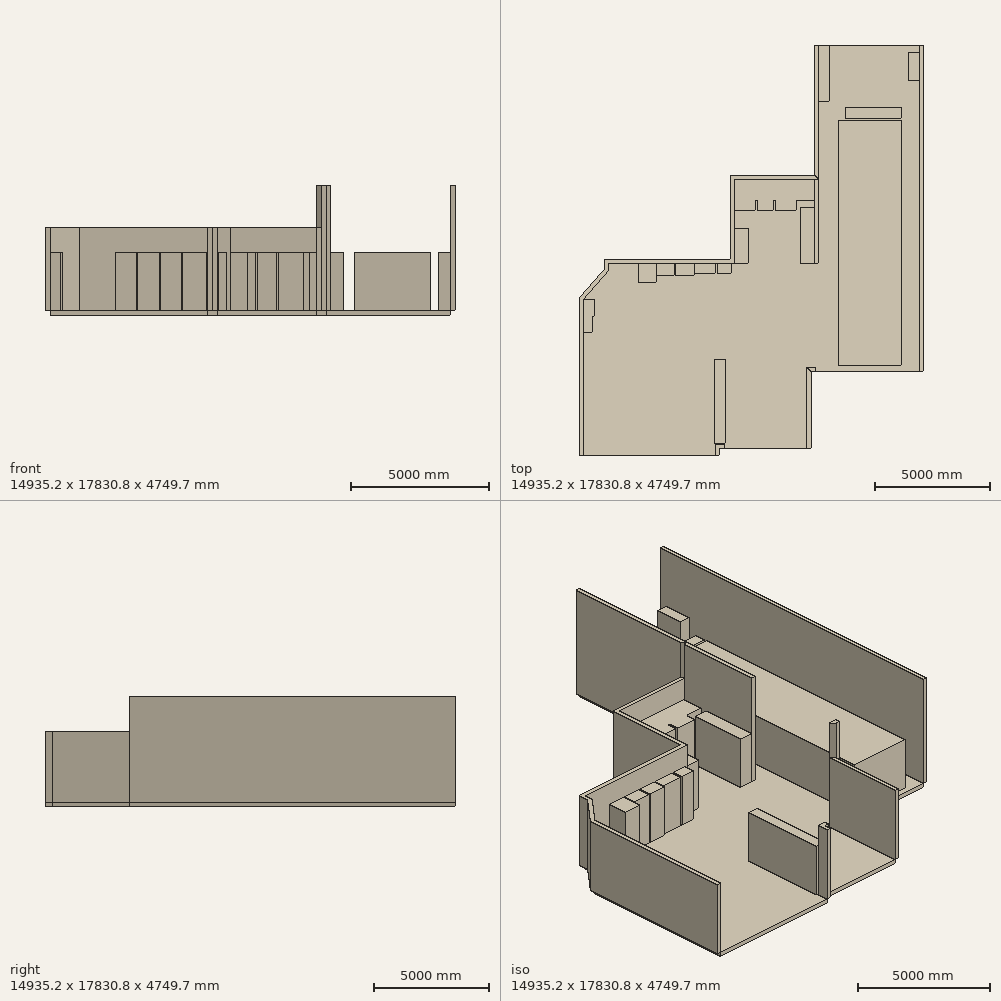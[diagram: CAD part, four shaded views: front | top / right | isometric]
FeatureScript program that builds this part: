
annotation { "Feature Type Name" : "Feature", "Feature Type Description" : "" }
export const myFeature = defineFeature(function(context is Context, id is Id, definition is map)
    precondition{}
    {
        {
            var Q0;
            Q0=qCreatedBy(makeId("Top.planeOp"),FACE);
            var sketch = newSketch(context, id + "F0", { "sketchPlane" : qUnion([Q0])});
            skLineSegment(sketch, "E0", {"start": v(0, 0) * mm, "end": v(6096, 0) * mm});
            skLineSegment(sketch, "E1", {"start": v(6096, 0) * mm, "end": v(6096, 304.8) * mm});
            skLineSegment(sketch, "E2", {"start": v(6096, 304.8) * mm, "end": v(10058.4, 304.8) * mm});
            skLineSegment(sketch, "E3", {"start": v(10058.4, 304.8) * mm, "end": v(10058.4, 3657.6) * mm});
            skLineSegment(sketch, "E4", {"start": v(10058.4, 3657.6) * mm, "end": v(14935.2, 3657.6) * mm});
            skLineSegment(sketch, "E5", {"start": v(14935.2, 3657.6) * mm, "end": v(14935.2, 17830.8) * mm});
            skLineSegment(sketch, "E6", {"start": v(14935.2, 17830.8) * mm, "end": v(10210.8, 17830.8) * mm});
            skLineSegment(sketch, "E7", {"start": v(10210.8, 17830.8) * mm, "end": v(10210.8, 12192) * mm});
            skLineSegment(sketch, "E8", {"start": v(10210.8, 12192) * mm, "end": v(6553.2, 12192) * mm});
            skLineSegment(sketch, "E9", {"start": v(6553.2, 12192) * mm, "end": v(6553.2, 8534.4) * mm});
            skLineSegment(sketch, "E10", {"start": v(0, 6858) * mm, "end": v(0, 0) * mm});
            skLineSegment(sketch, "E11", {"start": v(0, 6858) * mm, "end": v(1066.8, 8077.2) * mm});
            skLineSegment(sketch, "E12", {"start": v(1066.8, 8077.2) * mm, "end": v(1066.8, 8534.4) * mm});
            skLineSegment(sketch, "E13", {"start": v(1066.8, 8534.4) * mm, "end": v(6553.2, 8534.4) * mm});
            skLineSegment(sketch, "E14", {"start": v(177.7, 0) * mm, "end": v(177.7, 6791.23) * mm});
            skLineSegment(sketch, "E15", {"start": v(177.7, 6791.23) * mm, "end": v(1244.5, 8010.43) * mm});
            skLineSegment(sketch, "E16", {"start": v(1244.5, 8010.43) * mm, "end": v(1244.5, 8356.7) * mm});
            skLineSegment(sketch, "E17", {"start": v(1244.5, 8356.7) * mm, "end": v(6730.9, 8356.7) * mm});
            skLineSegment(sketch, "E18", {"start": v(6730.9, 8356.7) * mm, "end": v(6730.9, 12014.3) * mm});
            skLineSegment(sketch, "E19", {"start": v(6730.9, 12014.3) * mm, "end": v(10388.5, 12014.3) * mm});
            skLineSegment(sketch, "E20", {"start": v(10388.5, 12014.3) * mm, "end": v(10388.5, 17830.8) * mm});
            skLineSegment(sketch, "E21", {"start": v(10388.5, 17830.8) * mm, "end": v(14757.5, 17830.8) * mm});
            skLineSegment(sketch, "E22", {"start": v(9880.7, 3835.3) * mm, "end": v(9880.7, 304.8) * mm});
            skLineSegment(sketch, "E23", {"start": v(9880.7, 304.8) * mm, "end": v(6273.7, 304.8) * mm});
            skLineSegment(sketch, "E24", {"start": v(6273.7, 304.8) * mm, "end": v(6273.7, 482.5) * mm});
            skLineSegment(sketch, "E25", {"start": v(6273.7, 482.5) * mm, "end": v(5918.3, 482.5) * mm});
            skLineSegment(sketch, "E26", {"start": v(5918.3, 482.5) * mm, "end": v(5918.3, 0) * mm});
            skLineSegment(sketch, "E27", {"start": v(5918.3, 0) * mm, "end": v(177.7, 0) * mm});
            skLineSegment(sketch, "E28", {"start": v(14757.5, 17830.8) * mm, "end": v(14757.5, 3657.6) * mm});
            skLineSegment(sketch, "E29", {"start": v(14757.5, 3657.6) * mm, "end": v(10236.1, 3657.6) * mm});
            skLineSegment(sketch, "E30", {"start": v(10236.1, 3657.6) * mm, "end": v(10236.1, 3835.3) * mm});
            skLineSegment(sketch, "E31", {"start": v(10236.1, 3835.3) * mm, "end": v(9880.7, 3835.3) * mm});
            skLineSegment(sketch, "E32", {"start": v(10210.8, 12192) * mm, "end": v(10388.5, 12014.3) * mm});
            skLineSegment(sketch, "E33", {"start": v(10058.4, 3657.6) * mm, "end": v(9880.7, 3835.3) * mm});
            skLineSegment(sketch, "E34.bottom", {"start": v(10388.5, 12014.3) * mm, "end": v(10210.8, 12014.3) * mm});
            skLineSegment(sketch, "E34.top", {"start": v(10388.5, 8356.7) * mm, "end": v(10210.8, 8356.7) * mm});
            skLineSegment(sketch, "E34.left", {"start": v(10388.5, 12014.3) * mm, "end": v(10388.5, 8356.7) * mm});
            skLineSegment(sketch, "E34.right", {"start": v(10210.8, 12014.3) * mm, "end": v(10210.8, 8356.7) * mm});
            skSolve(sketch);
        }
        {
            var Q0;
            Q0=makeQuery(id+"F0.imprint","IMPRINT",FACE,{"disambiguationData":[TD([[makeQuery(id+"F0.imprint","IMPRINT",EDGE,{"derivedFrom":sQuery(id+"F0.wireOp",EDGE,"E8")}),1.0]])]});
            var Q1;
            {var subQ2=sQuery(id+"F0.wireOp",EDGE,"E1");Q1=makeQuery(id+"F0.imprint","IMPRINT",FACE,{"disambiguationData":[TD([[makeQuery(id+"F0.imprint","IMPRINT",EDGE,{"derivedFrom":subQ2}),1.0]])]});}
            var Q2;
            {var subQ0=sQuery(id+"F0.wireOp",EDGE,"E3");Q2=makeQuery(id+"F0.imprint","IMPRINT",FACE,{"disambiguationData":[TD([[makeQuery(id+"F0.imprint","IMPRINT",EDGE,{"derivedFrom":subQ0}),1.0]])]});}
            extrude(context, id + "F1", {"entities" : qUnion([Q0, Q1, Q2]), "depth" : 3048 * mm, "offsetDistance" : 30.48 * mm});
        }
        {
            var Q0;
            {var subQ0=sQuery(id+"F0.wireOp",EDGE,"E5");Q0=makeQuery(id+"F0.imprint","IMPRINT",FACE,{"disambiguationData":[TD([[makeQuery(id+"F0.imprint","IMPRINT",EDGE,{"derivedFrom":subQ0}),1.0]])]});}
            var Q1;
            {var subQ2=sQuery(id+"F0.wireOp",EDGE,"E30");Q1=makeQuery(id+"F0.imprint","IMPRINT",FACE,{"disambiguationData":[TD([[makeQuery(id+"F0.imprint","IMPRINT",EDGE,{"derivedFrom":subQ2}),1.0]])]});}
            var Q2;
            {var subQ0=sQuery(id+"F0.wireOp",EDGE,"E7");Q2=makeQuery(id+"F0.imprint","IMPRINT",FACE,{"disambiguationData":[TD([[makeQuery(id+"F0.imprint","IMPRINT",EDGE,{"derivedFrom":subQ0}),1.0]])]});}
            var Q3;
            Q3=makeQuery(id+"F0.imprint","IMPRINT",FACE,{"disambiguationData":[TD([[makeQuery(id+"F0.imprint","IMPRINT",EDGE,{"derivedFrom":sQuery(id+"F0.wireOp",EDGE,"E34.top")}),-1.0]])]});
            extrude(context, id + "F2", {"entities" : qUnion([Q0, Q1, Q2, Q3]), "depth" : 4572 * mm, "offsetDistance" : 30.48 * mm});
        }
        {
            var Q0;
            {var subQ6=sQuery(id+"F0.wireOp",EDGE,"E14");Q0=makeQuery(id+"F0.imprint","IMPRINT",FACE,{"disambiguationData":[TD([[makeQuery(id+"F0.imprint","IMPRINT",EDGE,{"derivedFrom":subQ6}),-1.0]])]});}
            extrude(context, id + "F3", {"entities" : qUnion([Q0]), "oppositeDirection" : true, "depth" : 177.7 * mm, "offsetDistance" : 30.48 * mm});
        }
        {
            var Q0;
            Q0=makeQuery(id+"F3.opExtrude","CAP_FACE",FACE,{"disambiguationData":[OSD([sQuery(id+"F0.wireOp",EDGE,"E0"),sQuery(id+"F0.wireOp",EDGE,"E2"),sQuery(id+"F0.wireOp",EDGE,"E4"),sQuery(id+"F0.wireOp",EDGE,"E6"),sQuery(id+"F0.wireOp",EDGE,"E14"),sQuery(id+"F0.wireOp",EDGE,"E15"),sQuery(id+"F0.wireOp",EDGE,"E16"),sQuery(id+"F0.wireOp",EDGE,"E17"),sQuery(id+"F0.wireOp",EDGE,"E18"),sQuery(id+"F0.wireOp",EDGE,"E19"),sQuery(id+"F0.wireOp",EDGE,"E20"),sQuery(id+"F0.wireOp",EDGE,"E22"),sQuery(id+"F0.wireOp",EDGE,"E24"),sQuery(id+"F0.wireOp",EDGE,"E25"),sQuery(id+"F0.wireOp",EDGE,"E26"),sQuery(id+"F0.wireOp",EDGE,"E28"),sQuery(id+"F0.wireOp",EDGE,"E30"),sQuery(id+"F0.wireOp",EDGE,"E31"),sQuery(id+"F0.wireOp",EDGE,"E34.top"),sQuery(id+"F0.wireOp",EDGE,"E34.left"),sQuery(id+"F0.wireOp",EDGE,"E34.right")])],"isStart":true});
            var sketch = newSketch(context, id + "F4", { "sketchPlane" : qUnion([Q0])});
            skLineSegment(sketch, "E35.bottom", {"start": v(2552.42, 8356.7) * mm, "end": v(3314.42, 8356.7) * mm});
            skLineSegment(sketch, "E35.top", {"start": v(2552.42, 7518.5) * mm, "end": v(3314.42, 7518.5) * mm});
            skLineSegment(sketch, "E35.left", {"start": v(2552.42, 8356.7) * mm, "end": v(2552.42, 7518.5) * mm});
            skLineSegment(sketch, "E35.right", {"start": v(3314.42, 8356.7) * mm, "end": v(3314.42, 7518.5) * mm});
            skLineSegment(sketch, "E36.bottom", {"start": v(3351.42, 8356.7) * mm, "end": v(4138.82, 8356.7) * mm});
            skLineSegment(sketch, "E36.top", {"start": v(3351.42, 7823.3) * mm, "end": v(4138.82, 7823.3) * mm});
            skLineSegment(sketch, "E36.left", {"start": v(3351.42, 8356.7) * mm, "end": v(3351.42, 7823.3) * mm});
            skLineSegment(sketch, "E36.right", {"start": v(4138.82, 8356.7) * mm, "end": v(4138.82, 7823.3) * mm});
            skLineSegment(sketch, "E37.bottom", {"start": v(4183.4, 8356.7) * mm, "end": v(4970.8, 8356.7) * mm});
            skLineSegment(sketch, "E37.top", {"start": v(4183.4, 7823.3) * mm, "end": v(4970.8, 7823.3) * mm});
            skLineSegment(sketch, "E37.left", {"start": v(4183.4, 8356.7) * mm, "end": v(4183.4, 7823.3) * mm});
            skLineSegment(sketch, "E37.right", {"start": v(4970.8, 8356.7) * mm, "end": v(4970.8, 7823.3) * mm});
            skLineSegment(sketch, "E38.bottom", {"start": v(5003.06, 8356.7) * mm, "end": v(5917.46, 8356.7) * mm});
            skLineSegment(sketch, "E38.top", {"start": v(5003.06, 7899.5) * mm, "end": v(5917.46, 7899.5) * mm});
            skLineSegment(sketch, "E38.left", {"start": v(5003.06, 8356.7) * mm, "end": v(5003.06, 7899.5) * mm});
            skLineSegment(sketch, "E38.right", {"start": v(5917.46, 8356.7) * mm, "end": v(5917.46, 7899.5) * mm});
            skLineSegment(sketch, "E39.bottom", {"start": v(6730.9, 12014.3) * mm, "end": v(10210.8, 12014.3) * mm});
            skLineSegment(sketch, "E39.top", {"start": v(6730.9, 11099.9) * mm, "end": v(10210.8, 11099.9) * mm});
            skLineSegment(sketch, "E39.left", {"start": v(6730.9, 12014.3) * mm, "end": v(6730.9, 11099.9) * mm});
            skLineSegment(sketch, "E39.right", {"start": v(10210.8, 12014.3) * mm, "end": v(10210.8, 11099.9) * mm});
            skLineSegment(sketch, "E40.bottom", {"start": v(5990.13, 8356.7) * mm, "end": v(6599.73, 8356.7) * mm});
            skLineSegment(sketch, "E40.top", {"start": v(5990.13, 7899.5) * mm, "end": v(6599.73, 7899.5) * mm});
            skLineSegment(sketch, "E40.left", {"start": v(5990.13, 8356.7) * mm, "end": v(5990.13, 7899.5) * mm});
            skLineSegment(sketch, "E40.right", {"start": v(6599.73, 8356.7) * mm, "end": v(6599.73, 7899.5) * mm});
            skLineSegment(sketch, "E41.bottom", {"start": v(6730.9, 11099.9) * mm, "end": v(7645.3, 11099.9) * mm});
            skLineSegment(sketch, "E41.top", {"start": v(6730.9, 10642.7) * mm, "end": v(7645.3, 10642.7) * mm});
            skLineSegment(sketch, "E41.left", {"start": v(6730.9, 11099.9) * mm, "end": v(6730.9, 10642.7) * mm});
            skLineSegment(sketch, "E41.right", {"start": v(7645.3, 11099.9) * mm, "end": v(7645.3, 10642.7) * mm});
            skLineSegment(sketch, "E42.bottom", {"start": v(8498.68, 11099.9) * mm, "end": v(9413.08, 11099.9) * mm});
            skLineSegment(sketch, "E42.top", {"start": v(8498.68, 10642.7) * mm, "end": v(9413.08, 10642.7) * mm});
            skLineSegment(sketch, "E42.left", {"start": v(8498.68, 11099.9) * mm, "end": v(8498.68, 10642.7) * mm});
            skLineSegment(sketch, "E42.right", {"start": v(9413.08, 11099.9) * mm, "end": v(9413.08, 10642.7) * mm});
            skLineSegment(sketch, "E43.bottom", {"start": v(10210.8, 8356.7) * mm, "end": v(9601.2, 8356.7) * mm});
            skLineSegment(sketch, "E43.top", {"start": v(10210.8, 10795.1) * mm, "end": v(9601.2, 10795.1) * mm});
            skLineSegment(sketch, "E43.left", {"start": v(10210.8, 8356.7) * mm, "end": v(10210.8, 10795.1) * mm});
            skLineSegment(sketch, "E43.right", {"start": v(9601.2, 8356.7) * mm, "end": v(9601.2, 10795.1) * mm});
            skLineSegment(sketch, "E44.bottom", {"start": v(7713.44, 11099.9) * mm, "end": v(8424.64, 11099.9) * mm});
            skLineSegment(sketch, "E44.top", {"start": v(7713.44, 10668.1) * mm, "end": v(8424.64, 10668.1) * mm});
            skLineSegment(sketch, "E44.left", {"start": v(7713.44, 11099.9) * mm, "end": v(7713.44, 10668.1) * mm});
            skLineSegment(sketch, "E44.right", {"start": v(8424.64, 11099.9) * mm, "end": v(8424.64, 10668.1) * mm});
            skLineSegment(sketch, "E45.bottom", {"start": v(6730.9, 8356.7) * mm, "end": v(7340.5, 8356.7) * mm});
            skLineSegment(sketch, "E45.top", {"start": v(6730.9, 9880.7) * mm, "end": v(7340.5, 9880.7) * mm});
            skLineSegment(sketch, "E45.left", {"start": v(6730.9, 8356.7) * mm, "end": v(6730.9, 9880.7) * mm});
            skLineSegment(sketch, "E45.right", {"start": v(7340.5, 8356.7) * mm, "end": v(7340.5, 9880.7) * mm});
            skLineSegment(sketch, "E46.bottom", {"start": v(5862.32, 1732.53) * mm, "end": v(6319.52, 1732.53) * mm});
            skLineSegment(sketch, "E46.top", {"start": v(5862.32, 513.33) * mm, "end": v(6319.52, 513.33) * mm});
            skLineSegment(sketch, "E46.left", {"start": v(5862.32, 1732.53) * mm, "end": v(5862.32, 513.33) * mm});
            skLineSegment(sketch, "E46.right", {"start": v(6319.52, 1732.53) * mm, "end": v(6319.52, 513.33) * mm});
            skLineSegment(sketch, "E47.bottom", {"start": v(5862.32, 2951.73) * mm, "end": v(6319.52, 2951.73) * mm});
            skLineSegment(sketch, "E47.left", {"start": v(5862.32, 2951.73) * mm, "end": v(5862.32, 1732.53) * mm});
            skLineSegment(sketch, "E47.right", {"start": v(6319.52, 2951.73) * mm, "end": v(6319.52, 1732.53) * mm});
            skLineSegment(sketch, "E48.top", {"start": v(5862.32, 4170.93) * mm, "end": v(6319.52, 4170.93) * mm});
            skLineSegment(sketch, "E48.left", {"start": v(5862.32, 2951.73) * mm, "end": v(5862.32, 4170.93) * mm});
            skLineSegment(sketch, "E48.right", {"start": v(6319.52, 2951.73) * mm, "end": v(6319.52, 4170.93) * mm});
            skLineSegment(sketch, "E49.bottom", {"start": v(177.7, 6791.23) * mm, "end": v(634.9, 6791.23) * mm});
            skLineSegment(sketch, "E49.top", {"start": v(177.7, 6054.63) * mm, "end": v(634.9, 6054.63) * mm});
            skLineSegment(sketch, "E49.left", {"start": v(177.7, 6791.23) * mm, "end": v(177.7, 6054.63) * mm});
            skLineSegment(sketch, "E49.right", {"start": v(634.9, 6791.23) * mm, "end": v(634.9, 6054.63) * mm});
            skLineSegment(sketch, "E50.bottom", {"start": v(177.7, 6054.63) * mm, "end": v(558.7, 6054.63) * mm});
            skLineSegment(sketch, "E50.top", {"start": v(177.7, 5343.43) * mm, "end": v(558.7, 5343.43) * mm});
            skLineSegment(sketch, "E50.left", {"start": v(177.7, 6054.63) * mm, "end": v(177.7, 5343.43) * mm});
            skLineSegment(sketch, "E50.right", {"start": v(558.7, 6054.63) * mm, "end": v(558.7, 5343.43) * mm});
            skLineSegment(sketch, "E51.bottom", {"start": v(11268.81, 14570.97) * mm, "end": v(14012.01, 14570.97) * mm});
            skLineSegment(sketch, "E51.top", {"start": v(11268.81, 3902.97) * mm, "end": v(14012.01, 3902.97) * mm});
            skLineSegment(sketch, "E51.left", {"start": v(11268.81, 14570.97) * mm, "end": v(11268.81, 3902.97) * mm});
            skLineSegment(sketch, "E51.right", {"start": v(14012.01, 14570.97) * mm, "end": v(14012.01, 3902.97) * mm});
            skLineSegment(sketch, "E52.bottom", {"start": v(11544.94, 15133.54) * mm, "end": v(12764.14, 15133.54) * mm});
            skLineSegment(sketch, "E52.top", {"start": v(11544.94, 14676.34) * mm, "end": v(12764.14, 14676.34) * mm});
            skLineSegment(sketch, "E52.left", {"start": v(11544.94, 15133.54) * mm, "end": v(11544.94, 14676.34) * mm});
            skLineSegment(sketch, "E52.right", {"start": v(12764.14, 15133.54) * mm, "end": v(12764.14, 14676.34) * mm});
            skLineSegment(sketch, "E53.bottom", {"start": v(12764.14, 15133.54) * mm, "end": v(13983.34, 15133.54) * mm});
            skLineSegment(sketch, "E53.top", {"start": v(12764.14, 14676.34) * mm, "end": v(13983.34, 14676.34) * mm});
            skLineSegment(sketch, "E54.left", {"start": v(13983.34, 15133.54) * mm, "end": v(13983.34, 14676.34) * mm});
            skLineSegment(sketch, "E55.bottom", {"start": v(10388.5, 17830.8) * mm, "end": v(10845.7, 17830.8) * mm});
            skLineSegment(sketch, "E55.top", {"start": v(10388.5, 16611.6) * mm, "end": v(10845.7, 16611.6) * mm});
            skLineSegment(sketch, "E55.left", {"start": v(10388.5, 17830.8) * mm, "end": v(10388.5, 16611.6) * mm});
            skLineSegment(sketch, "E55.right", {"start": v(10845.7, 17830.8) * mm, "end": v(10845.7, 16611.6) * mm});
            skLineSegment(sketch, "E56.top", {"start": v(10388.5, 15392.4) * mm, "end": v(10845.7, 15392.4) * mm});
            skLineSegment(sketch, "E56.left", {"start": v(10388.5, 16611.6) * mm, "end": v(10388.5, 15392.4) * mm});
            skLineSegment(sketch, "E56.right", {"start": v(10845.7, 16611.6) * mm, "end": v(10845.7, 15392.4) * mm});
            skLineSegment(sketch, "E57.bottom", {"start": v(14757.5, 16295.14) * mm, "end": v(14300.3, 16295.14) * mm});
            skLineSegment(sketch, "E57.top", {"start": v(14757.5, 17514.34) * mm, "end": v(14300.3, 17514.34) * mm});
            skLineSegment(sketch, "E57.left", {"start": v(14757.5, 16295.14) * mm, "end": v(14757.5, 17514.34) * mm});
            skLineSegment(sketch, "E57.right", {"start": v(14300.3, 16295.14) * mm, "end": v(14300.3, 17514.34) * mm});
            skSolve(sketch);
        }
        {
            var Q0;
            Q0 = qSketchRegion(id + "F4", true);
            extrude(context, id + "F5", {"entities" : qUnion([Q0]), "depth" : 2133.6 * mm, "offsetDistance" : 30.48 * mm});
        }
    });
